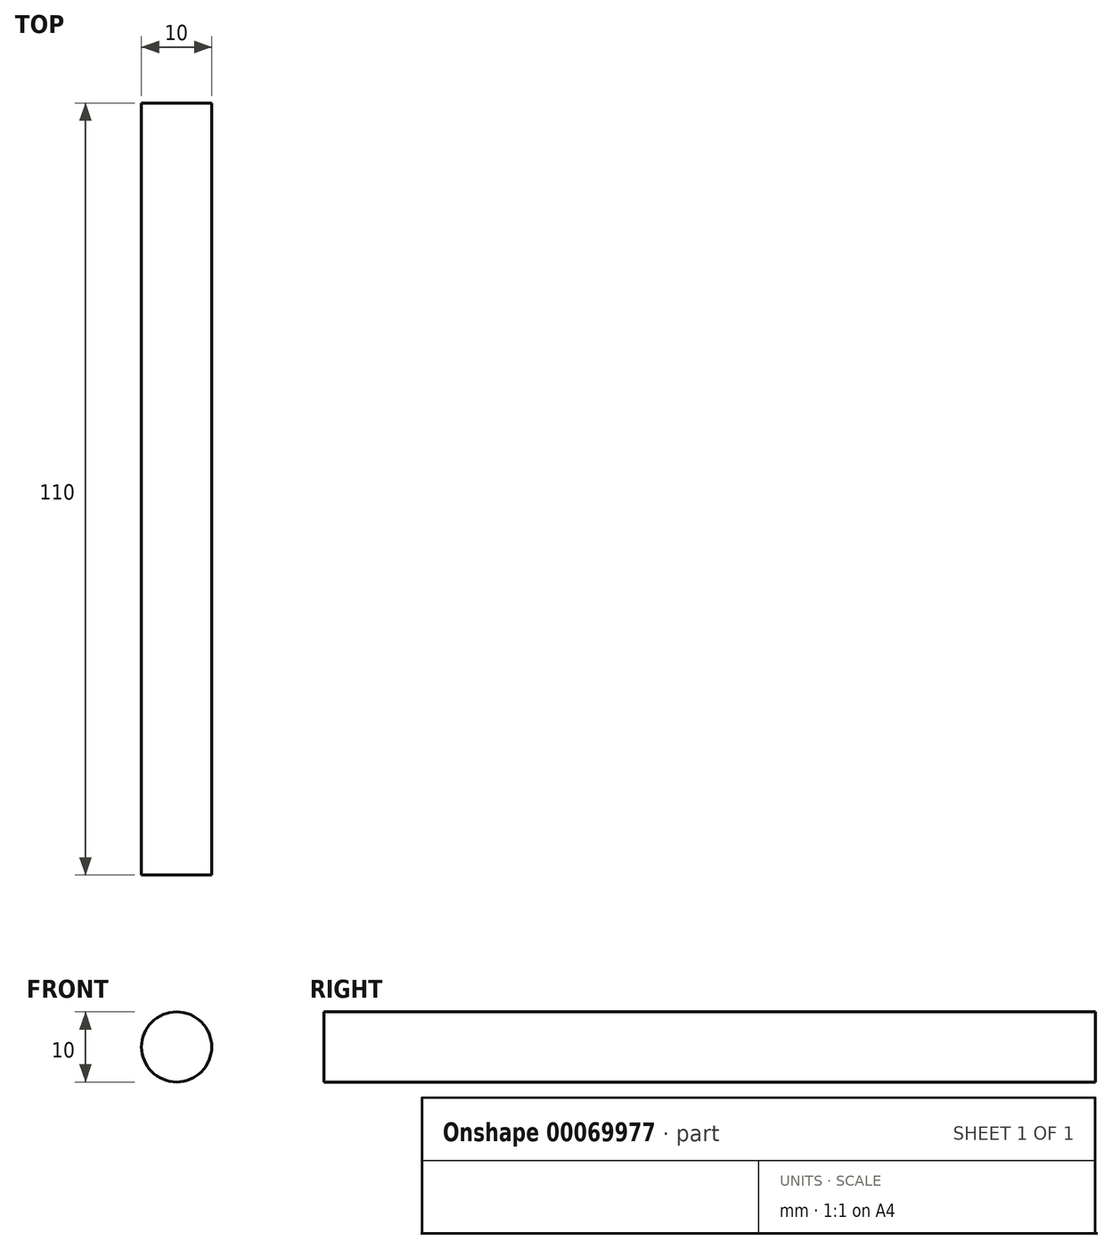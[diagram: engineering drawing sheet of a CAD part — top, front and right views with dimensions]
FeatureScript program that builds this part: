
annotation { "Feature Type Name" : "Feature", "Feature Type Description" : "" }
export const myFeature = defineFeature(function(context is Context, id is Id, definition is map)
    precondition{}
    {
        {
            var Q0;
            Q0=qCreatedBy(makeId("Front.planeOp"),FACE);
            var sketch = newSketch(context, id + "F0", { "sketchPlane" : qUnion([Q0])});
            skCircle(sketch, "E0", {"center": v(0, 0) * mm, "radius": 5 * mm});
            skSolve(sketch);
        }
        {
            var Q0;
            Q0=makeQuery(id+"F0.imprint","IMPRINT",FACE,{"disambiguationData":[TD([[makeQuery(id+"F0.imprint","IMPRINT",EDGE,{"derivedFrom":sQuery(id+"F0.wireOp",EDGE,"E0")}),1.0]])]});
            extrude(context, id + "F1", {"entities" : qUnion([Q0]), "depth" : 110 * mm});
        }
    });
